# Revit family: 506_VCF-C-_-E-ZP-0-0
name_source: partatom
category: Electrical Equipment
revit_build: Autodesk Revit 2018 (Build: 20170223_1515(x64)
units: mm (PartAtom-declared; Revit-internal decimal feet)

## family parameters
Always vertical = Yes
Cut with Voids When Loaded = No
Part Type = Equipment Switch
Room Calculation Point = No
Round Connector Dimension = Use Diameter
Shared = No
Work Plane-Based = No

## types (4) — shared parameters
CAT0 = Yes
Description = Air curtain FINESSE, output series C, electric heater
H2 = 299 mm  [stored 0.980971 ft]
H2__ve = -299 mm  [stored -0.980971 ft]
H3 = 2 mm  [stored 0.00656168 ft]
H3__ve = -2 mm  [stored -0.00656168 ft]
MC Active Power = 1 W
MC CosPhi = 0.95
MC Number of Poles = 3
MC Voltage = 0 V
Manufacturer = 2VV
URL = www.2vv.cz
W3 = 298 mm  [stored 0.97769 ft]
W5 = 319 mm  [stored 1.04659 ft]
W6 = 119 mm
W7 = 179 mm
W8 = 89 mm
magiApparentLoad = 1 VA
magiPartTypeId = 506
magiProductFamilyId = VCF-C-*-E-ZP-0-0
zero-valued in all types: L2D, W2D

## per-type parameters (varying)
| type | A1 | B1 | L4 |
| VCF-C-100-E-ZP-0-0 | 528 mm | 562 mm  [stored 1.84383 ft] | 583 mm  [stored 1.91273 ft] |
| VCF-C-250-E-ZP-0-0 | 1218 mm | 1252 mm | 1273 mm |
| VCF-C-200-E-ZP-0-0 | 1028 mm | 1062 mm | 1083 mm |
| VCF-C-150-E-ZP-0-0 | 778 mm | 812 mm | 833 mm |

note: column(s) folded — value = type name in every type: MC Product Code, magiProductId

note: [stored X ft] marks values corroborated as IEEE doubles in the binary element streams (Revit-internal decimal feet)

## geometry (parser evidence)
native form markers: Blend x4, Sweep x2
no freeform markers — native parametric forms only
